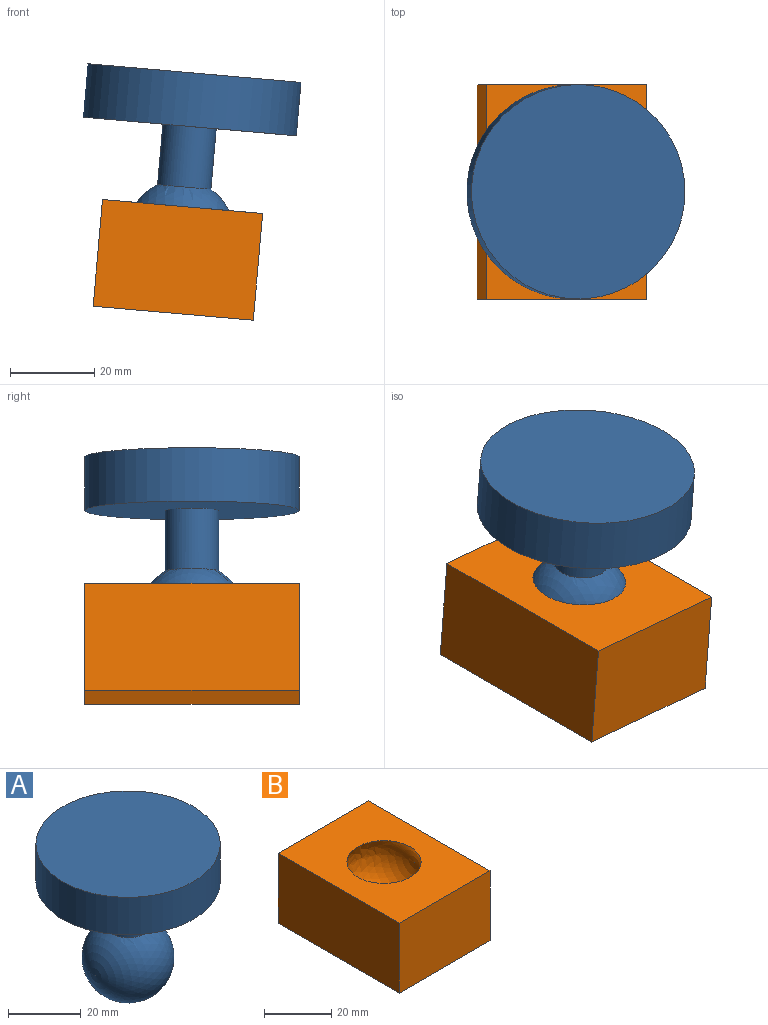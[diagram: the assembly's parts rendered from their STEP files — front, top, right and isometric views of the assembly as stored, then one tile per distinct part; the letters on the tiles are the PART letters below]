
ASSEMBLY  parts=2 mates=1
PART A: 5 faces, bbox 50.8x50.8x50.8 mm
  f0: sphere r=12.7mm, area 1891.1mm2, adj f1
  f1: cylinder r=6.35mm len=14.4mm, axis (0,0,-1), area 574.6mm2, adj f0,f4
  f2: cylinder r=25.4mm len=50.8mm, axis (0,0,-1), area 2026.8mm2, adj f3,f4
  f3: plane 50.8x50.8mm, normal (0,0,1), area 2026.8mm2, adj f2
  f4: plane 50.8x50.8mm, normal (0,0,-1), area 1900.2mm2, adj f1,f2
PART B: 7 faces, bbox 38.1x50.8x31.8 mm
  f0: plane 38.1x25.4mm, normal (0,-1,0), area 967.7mm2, adj f1,f3,f4,f5
  f1: plane 50.8x25.4mm, normal (1,0,0), area 1290.3mm2, adj f0,f2,f4,f5
  f2: plane 38.1x25.4mm, normal (0,1,0), area 967.7mm2, adj f1,f3,f4,f5
  f3: plane 50.8x25.4mm, normal (-1,0,0), area 1290.3mm2, adj f0,f2,f4,f5
  f4: plane 50.8x38.1mm, normal (0,0,1), area 1555.4mm2, adj f0,f1,f2,f3,f6
  f5: plane 50.8x38.1mm, normal (0,0,-1), area 1935.5mm2, adj f0,f1,f2,f3
  f6: sphere r=12.7mm, area 1520.1mm2, adj f4
PLACE A rot(axis=(0,1,0),5deg) t=(-4.1,-2.15,15.75)mm
PLACE B rot(axis=(0,1,0),5deg) t=(-5.76,-2.15,-3.23)mm
MATE ball A.f1 <-> B.f6  axis (0.09,0,1) through (-4.1,-2.15,15.75)mm
